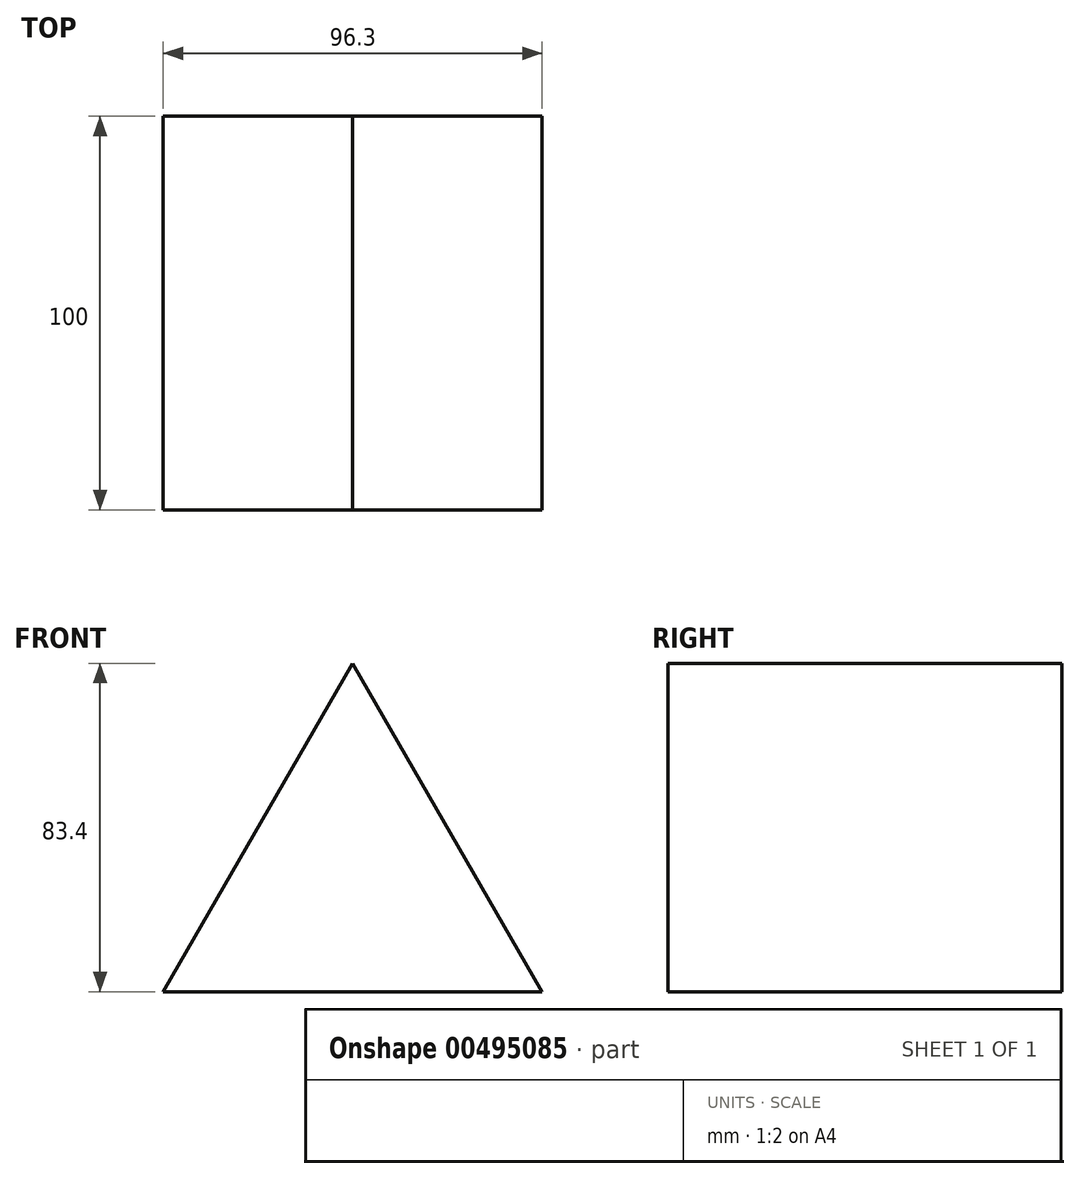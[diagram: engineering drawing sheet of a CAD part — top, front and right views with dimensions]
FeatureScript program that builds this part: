
annotation { "Feature Type Name" : "Feature", "Feature Type Description" : "" }
export const myFeature = defineFeature(function(context is Context, id is Id, definition is map)
    precondition{}
    {
        {
            var Q0;
            Q0=qCreatedBy(makeId("Front.planeOp"),FACE);
            var sketch = newSketch(context, id + "F0", { "sketchPlane" : qUnion([Q0])});
            skCircle(sketch, "E0.cCircle", {"center": v(0, 0) * mm, "radius": 55.6 * mm, "construction": true});
            skLineSegment(sketch, "E0.0", {"start": v(48.15, -27.8) * mm, "end": v(-48.15, -27.8) * mm});
            skLineSegment(sketch, "E0.1", {"start": v(-48.15, -27.8) * mm, "end": v(0, 55.6) * mm});
            skLineSegment(sketch, "E0.2", {"start": v(0, 55.6) * mm, "end": v(48.15, -27.8) * mm});
            skSolve(sketch);
        }
        {
            var Q0;
            Q0 = qSketchRegion(id + "F0", true);
            extrude(context, id + "F1", {"entities" : qUnion([Q0]), "depth" : 100 * mm});
        }
    });
